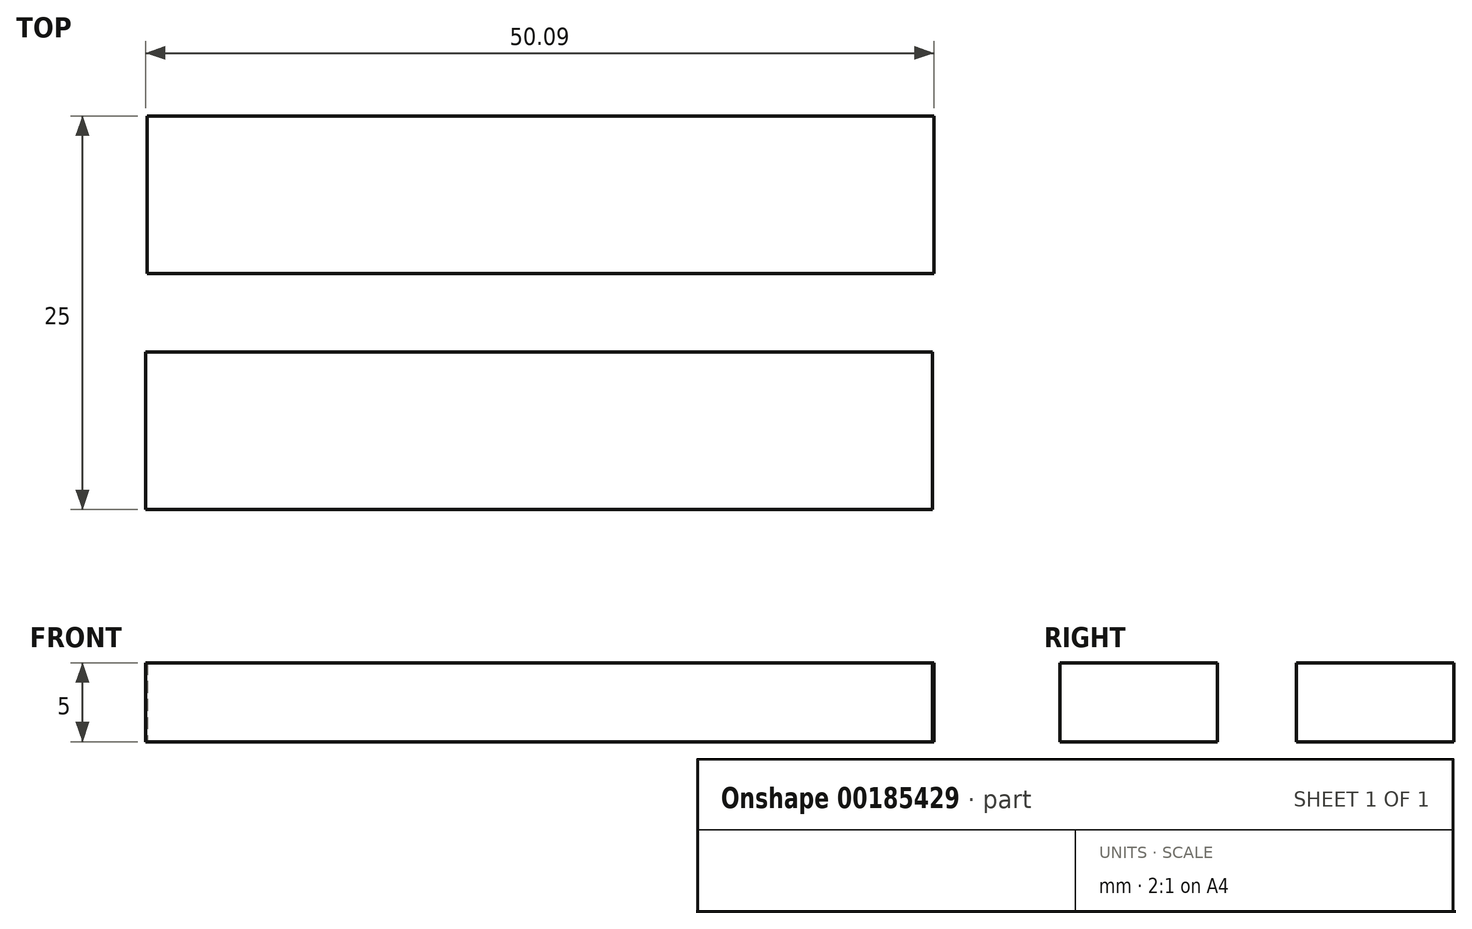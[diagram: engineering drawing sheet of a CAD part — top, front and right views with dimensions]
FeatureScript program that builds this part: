
annotation { "Feature Type Name" : "Feature", "Feature Type Description" : "" }
export const myFeature = defineFeature(function(context is Context, id is Id, definition is map)
    precondition{}
    {
        {
            var Q0;
            Q0=qCreatedBy(makeId("Top.planeOp"),FACE);
            var sketch = newSketch(context, id + "F0", { "sketchPlane" : qUnion([Q0])});
            skLineSegment(sketch, "E0.bottom", {"start": v(25, 5) * mm, "end": v(-25, 5) * mm});
            skLineSegment(sketch, "E0.top", {"start": v(25, -5) * mm, "end": v(-25, -5) * mm});
            skLineSegment(sketch, "E0.left", {"start": v(25, 5) * mm, "end": v(25, -5) * mm});
            skLineSegment(sketch, "E0.right", {"start": v(-25, 5) * mm, "end": v(-25, -5) * mm});
            skPoint(sketch, "E0.middle", {"position": v(0, 0) * mm});
            skLineSegment(sketch, "E1.1.0.0", {"start": v(25.1, 20) * mm, "end": v(-24.9, 20) * mm});
            skLineSegment(sketch, "E1.1.0.1", {"start": v(-24.9, 20) * mm, "end": v(-24.9, 10) * mm});
            skLineSegment(sketch, "E1.1.0.2", {"start": v(25.1, 10) * mm, "end": v(-24.9, 10) * mm});
            skLineSegment(sketch, "E1.1.0.3", {"start": v(25.1, 20) * mm, "end": v(25.1, 10) * mm});
            skLineSegment(sketch, "E1.direction1", {"start": v(-25, 5) * mm, "end": v(-24.9, 20) * mm, "construction": true});
            skSolve(sketch);
        }
        {
            var Q0;
            Q0 = qSketchRegion(id + "F0", true);
            extrude(context, id + "F1", {"entities" : qUnion([Q0]), "depth" : 5 * mm});
        }
    });
